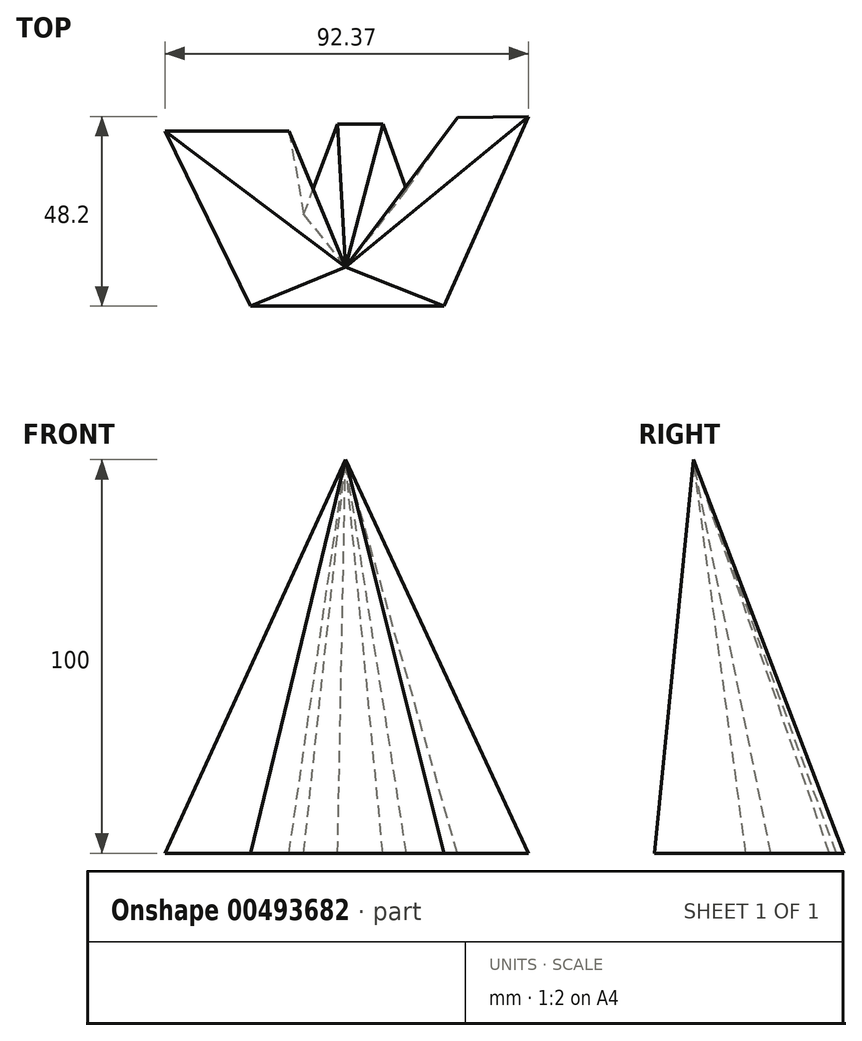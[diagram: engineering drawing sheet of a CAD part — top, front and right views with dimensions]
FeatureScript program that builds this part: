
annotation { "Feature Type Name" : "Feature", "Feature Type Description" : "" }
export const myFeature = defineFeature(function(context is Context, id is Id, definition is map)
    precondition{}
    {
        {
            var Q0;
            Q0=qCreatedBy(makeId("Top.planeOp"),FACE);
            var sketch = newSketch(context, id + "F0", { "sketchPlane" : qUnion([Q0])});
            skLineSegment(sketch, "E0", {"start": v(-43.9, 34.57) * mm, "end": v(-12.34, 34.57) * mm});
            skLineSegment(sketch, "E1", {"start": v(-12.34, 34.57) * mm, "end": v(-8.6, 13.34) * mm});
            skLineSegment(sketch, "E2", {"start": v(-8.6, 13.34) * mm, "end": v(0, 36.3) * mm});
            skLineSegment(sketch, "E3", {"start": v(0, 36.3) * mm, "end": v(11.48, 36.3) * mm});
            skLineSegment(sketch, "E4", {"start": v(11.48, 36.3) * mm, "end": v(17.5, 19.65) * mm});
            skLineSegment(sketch, "E5", {"start": v(17.5, 19.65) * mm, "end": v(30.4, 38.01) * mm});
            skLineSegment(sketch, "E6", {"start": v(30.4, 38.01) * mm, "end": v(48.48, 38.3) * mm});
            skLineSegment(sketch, "E7", {"start": v(48.48, 38.3) * mm, "end": v(26.97, -9.9) * mm});
            skLineSegment(sketch, "E8", {"start": v(26.97, -9.9) * mm, "end": v(-22.1, -9.9) * mm});
            skLineSegment(sketch, "E9", {"start": v(-22.1, -9.9) * mm, "end": v(-43.9, 34.57) * mm});
            skSolve(sketch);
        }
        {
            var Q0;
            Q0=qCreatedBy(makeId("Top.planeOp"),FACE);
            cPlane(context, id + "F1", {"entities" : qUnion([Q0]), "cplaneType" : CPlaneType.OFFSET, "offset" : 100 * mm, "width" : 150 * mm, "height" : 150 * mm});
        }
        {
            var Q0;
            Q0=qCreatedBy(id+"F1.planeOp",FACE);
            var sketch = newSketch(context, id + "F2", { "sketchPlane" : qUnion([Q0])});
            skPoint(sketch, "E10", {"position": v(2, 0) * mm});
            skSolve(sketch);
        }
        {
            var Q0;
            Q0=makeQuery(id+"F0.imprint","IMPRINT",FACE,{"disambiguationData":[TD([[makeQuery(id+"F0.imprint","IMPRINT",EDGE,{"derivedFrom":sQuery(id+"F0.wireOp",EDGE,"E0")}),-1.0]])]});
            var Q1;
            Q1=sQuery(id+"F2.wireOp",VERTEX,"E10");
            loft(context, id + "F3", {"sheetProfilesArray" : [{ "sheetProfileEntities" : qUnion([Q0]) }, { "sheetProfileEntities" : qUnion([Q1]) }]});
        }
    });
